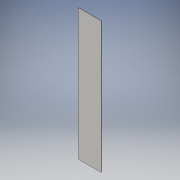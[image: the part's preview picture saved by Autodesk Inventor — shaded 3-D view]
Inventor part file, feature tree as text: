
AUTODESK INVENTOR PART (.ipt)
format: ipt  version: 2016 (Build 200138000, 138)  size: 88,064 bytes
history: native  units: in
note: dims shown in document units (in); Inventor stores cm internally (conversion verified against a paired STEP export)
features: extrude x1, sketch x1
ambient origin geometry x8: Origin, YZ Plane, XZ Plane, XY Plane, X Axis, Y Axis, Z Axis, Center Point
bodies: Solid1 (feature_tree)
feature tree (2):
  extrude  "Extrusion1"  Depth=17.5in
  sketch  "Sketch1"  dims[d0=3.0in d1=17.5in d2=0.0625in d3=0.0in]
